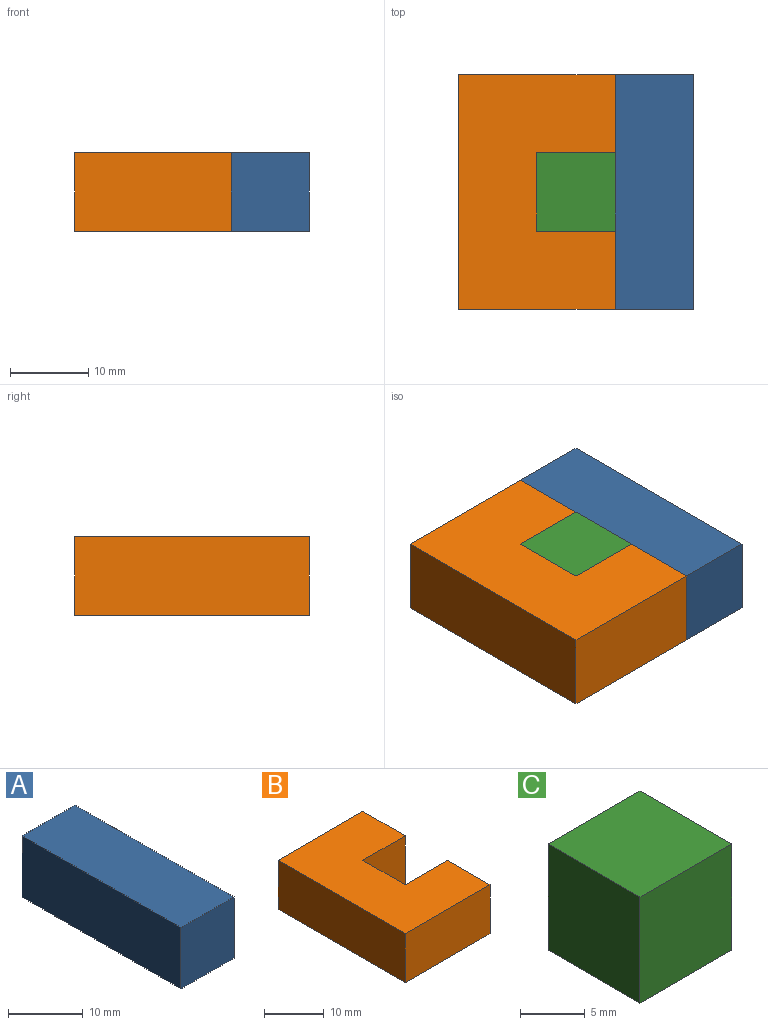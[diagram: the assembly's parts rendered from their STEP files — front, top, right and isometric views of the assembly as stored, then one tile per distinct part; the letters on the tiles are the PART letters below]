
ASSEMBLY  parts=3 mates=2
PART A: 6 faces, bbox 10x30x10 mm
  f0: plane 10x10mm, normal (0,1,0), area 100mm2, adj f1,f3,f4,f5
  f1: plane 30x10mm, normal (-1,0,0), area 300mm2, adj f0,f2,f4,f5
  f2: plane 10x10mm, normal (0,-1,0), area 100mm2, adj f1,f3,f4,f5
  f3: plane 30x10mm, normal (1,0,0), area 300mm2, adj f0,f2,f4,f5
  f4: plane 30x10mm, normal (0,0,1), area 300mm2, adj f0,f1,f2,f3
  f5: plane 30x10mm, normal (0,0,-1), area 300mm2, adj f0,f1,f2,f3
PART B: 10 faces, bbox 20x30x10 mm
  f0: plane 20x10mm, normal (0,1,0), area 200mm2, adj f1,f7,f8,f9
  f1: plane 30x10mm, normal (-1,0,0), area 300mm2, adj f0,f2,f8,f9
  f2: plane 20x10mm, normal (0,-1,0), area 200mm2, adj f1,f3,f8,f9
  f3: plane 10x10mm, normal (1,0,0), area 100mm2, adj f2,f4,f8,f9
  f4: plane 10x10mm, normal (0,1,0), area 100mm2, adj f3,f5,f8,f9
  f5: plane 10x10mm, normal (1,0,0), area 100mm2, adj f4,f6,f8,f9
  f6: plane 10x10mm, normal (0,-1,0), area 100mm2, adj f5,f7,f8,f9
  f7: plane 10x10mm, normal (1,0,0), area 100mm2, adj f0,f6,f8,f9
  f8: plane 30x20mm, normal (0,0,1), area 500mm2, adj f0,f1,f2,f3,f4,f5,f6,f7
  f9: plane 30x20mm, normal (0,0,-1), area 500mm2, adj f0,f1,f2,f3,f4,f5,f6,f7
PART C: 6 faces, bbox 10x10x10 mm
  f0: plane 10x10mm, normal (0,1,0), area 100mm2, adj f1,f3,f4,f5
  f1: plane 10x10mm, normal (-1,0,0), area 100mm2, adj f0,f2,f4,f5
  f2: plane 10x10mm, normal (0,-1,0), area 100mm2, adj f1,f3,f4,f5
  f3: plane 10x10mm, normal (1,0,0), area 100mm2, adj f0,f2,f4,f5
  f4: plane 10x10mm, normal (0,0,1), area 100mm2, adj f0,f1,f2,f3
  f5: plane 10x10mm, normal (0,0,-1), area 100mm2, adj f0,f1,f2,f3
PLACE A t=(31.36,15.03,-41.36)mm
PLACE B t=(11.36,10.59,-41.36)mm
PLACE C t=(-8.08,31.41,-41.36)mm
MATE fastened B.f9 <-> C.f5  axis (0,0,-1) through (21.36,6.77,-41.36)mm
MATE fastened C.f5 <-> A.f5  axis (0,0,-1) through (31.36,6.77,-41.36)mm
